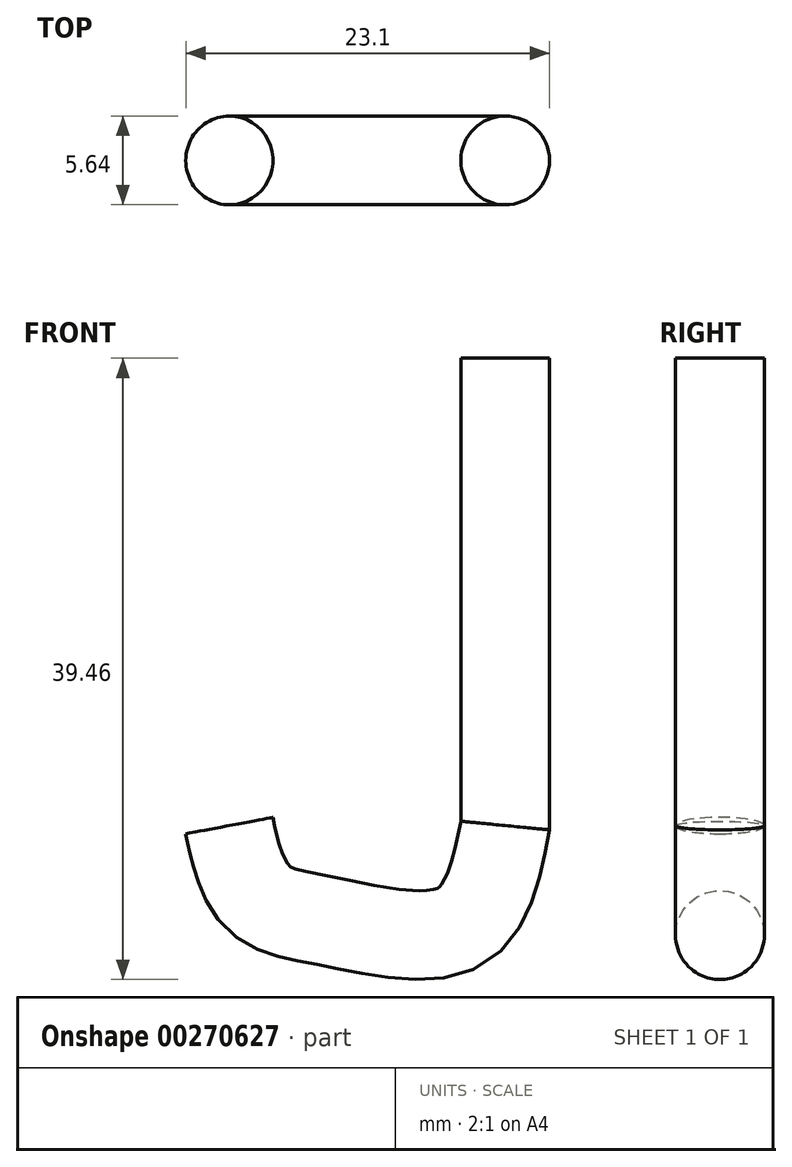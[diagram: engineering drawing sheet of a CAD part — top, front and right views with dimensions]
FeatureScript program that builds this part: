
annotation { "Feature Type Name" : "Feature", "Feature Type Description" : "" }
export const myFeature = defineFeature(function(context is Context, id is Id, definition is map)
    precondition{}
    {
        {
            var Q0;
            Q0=qCreatedBy(makeId("Front.planeOp"),FACE);
            var sketch = newSketch(context, id + "F0", { "sketchPlane" : qUnion([Q0])});
            skLineSegment(sketch, "E0", {"start": v(0, 0) * mm, "end": v(0, -29.68) * mm});
            skFitSpline(sketch, "E1", {"points": [v(0, -29.68) * mm, v(-2.95, -36.13) * mm, v(-11.25, -35.76) * mm, v(-15.67, -34.3) * mm, v(-17.15, -31.34) * mm, v(-17.51, -29.68) * mm], "startDerivative": vector(-6.54, -33.2) * mm, "endDerivative": vector(-2.33, 12.35) * mm});
            skSolve(sketch);
        }
        {
            var Q0;
            Q0=qCreatedBy(makeId("Top.planeOp"),FACE);
            var sketch = newSketch(context, id + "F1", { "sketchPlane" : qUnion([Q0])});
            skCircle(sketch, "E2", {"center": v(0, 0) * mm, "radius": 2.82 * mm});
            skSolve(sketch);
        }
        {
            var Q0;
            Q0=makeQuery(id+"F1.imprint","IMPRINT",FACE,{"disambiguationData":[TD([[makeQuery(id+"F1.imprint","IMPRINT",EDGE,{"derivedFrom":sQuery(id+"F1.wireOp",EDGE,"E2")}),1.0]])]});
            var Q1;
            Q1=sQuery(id+"F0.wireOp",EDGE,"E0");
            var Q2;
            Q2=sQuery(id+"F0.wireOp",EDGE,"E1");
            sweep(context, id + "F2", {"profiles" : qUnion([Q0]), "path" : qUnion([Q1, Q2])});
        }
    });
